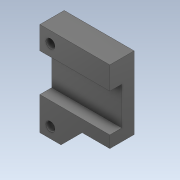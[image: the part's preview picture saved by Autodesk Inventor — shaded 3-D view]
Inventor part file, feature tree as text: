
AUTODESK INVENTOR PART (.ipt)
format: ipt  version: 2020 (Build 240168000, 168)  size: 666,112 bytes
history: native  units: mm
features: extrude x31, sketch x29, projected_geometry x21, reference x8, other x5, chamfer x4, plane x1, hole x1
ambient origin geometry x8: Origin, YZ Plane, XZ Plane, XY Plane, X Axis, Y Axis, Z Axis, Center Point
bodies: Solid1 (feature_tree)
feature tree (100):
  extrude  "Extrusion1"  Depth=45.0mm
  plane  "Work Plane1"
  extrude  "Extrusion2"  Depth=18.0mm
  extrude  "Extrusion3"  Depth=2.0mm TaperAngle=0.0deg
  extrude  "Extrusion4"  TaperAngle=0.0deg  [1 undecoded]
  extrude  "Extrusion5"  Depth=50.1mm TaperAngle=0.0deg
  sketch  "Sketch6"  dims[d14=7.199887mm d15=3.599976mm]
  extrude  "Extrusion6"  Depth=3.599976mm
  extrude  "Extrusion7"  Depth=0.15mm
  extrude  "Extrusion8"  Depth=0.15mm
  extrude  "Extrusion10"  Depth=15.9mm TaperAngle=0.0deg
  extrude  "Extrusion11"  Depth=23.15mm
  extrude  "Extrusion12"  Depth=3.925mm
  extrude  "Extrusion13"  Depth=5.15mm
  sketch  "Sketch14"  dims[d29=2.525mm d30=5.15mm]
  extrude  "Extrusion14"  Depth=12.55mm
  extrude  "Extrusion15"  Depth=2.75mm TaperAngle=0.0deg
  hole  "Hole1"  [1 undecoded]
  extrude  "Extrusion16"  Depth=3.925mm
  extrude  "Extrusion18"  Depth=23.15mm
  extrude  "Extrusion20"  Depth=10.0mm
  extrude  "Extrusion21"  Depth=0.0mm
  extrude  "Extrusion22"  TaperAngle=0.0deg  [1 undecoded]
  chamfer  "Chamfer1"  Distance=12.55mm
  extrude  "Extrusion23"  Depth=10.0mm
  extrude  "Extrusion24"  Depth=0.5mm
  chamfer  "Chamfer2"  Distance=17.225mm
  extrude  "Extrusion25"  Depth=4.0mm TaperAngle=0.0deg
  extrude  "Extrusion26"  Depth=0.5mm
  extrude  "Extrusion28"  Depth=10.925mm
  extrude  "Extrusion31"  Depth=0.5mm TaperAngle=0.0deg
  extrude  "Extrusion32"  Depth=0.5mm
  extrude  "Extrusion35"  Depth=0.5mm TaperAngle=0.0deg
  extrude  "Extrusion36"  Depth=0.5mm
  extrude  "Extrusion37"  Depth=0.5mm
  extrude  "Extrusion38"  Depth=0.5mm
  chamfer  "Chamfer4"  Distance=53.1mm
  chamfer  "Chamfer6"  Distance=53.1mm
  extrude  "Extrusion39"  Depth=0.5mm
  sketch  "Sketch1"  dims[d0=18.0mm d1=45.0mm]
  reference  "Reference1"
  sketch  "Sketch2"  dims[d2=45.0mm d3=18.0mm]
  reference  "Reference2"
  sketch  "Sketch3"  dims[d4=18.0mm d5=51.1mm d6=2.0mm d7=0.0mm d8=0.0mm]
  reference  "Reference3"
  reference  "Reference4"
  reference  "Reference5"
  reference  "Reference6"
  reference  "Reference7"
  reference  "Reference8"
  sketch  "Sketch4"  dims[d9=37.3mm d10=0.0mm]
  sketch  "Sketch5"  dims[d11=35.0mm d12=50.1mm d13=0.0mm]
  sketch  "Sketch8"  dims[d16=0.15mm d17=0.15mm]
  sketch  "Sketch10"  dims[d18=0.15mm d19=0.15mm]
  sketch  "Sketch11"  dims[d20=5.4mm d21=0.0mm d22=15.9mm d23=0.0mm]
  sketch  "Sketch12"  dims[d24=6.5mm d25=0.0mm d26=23.15mm]
  sketch  "Sketch13"  dims[d27=12.55mm d28=3.925mm]
  sketch  "Sketch15"  dims[d31=5.15mm d32=12.55mm]
  sketch  "Sketch17"  dims[d33=40.75mm d34=0.0mm d35=2.75mm d36=0.0mm]
  sketch  "Sketch19"  dims[d43=11.85mm d44=23.15mm]
  projected_geometry  "Projected Loop1"
  sketch  "Sketch21"  dims[d45=3.925mm d46=2.525mm]
  projected_geometry  "Projected Loop3"
  sketch  "Sketch22"  dims[d47=12.55mm d48=23.15mm]
  sketch  "Sketch23"  dims[d49=10.05mm d50=0.0mm d54=10.0mm]
  projected_geometry  "Projected Loop4"
  projected_geometry  "Projected Loop5"
  projected_geometry  "Projected Loop6"
  projected_geometry  "Projected Loop7"
  sketch  "Sketch24"  dims[d55=0.0mm d56=0.0mm]
  projected_geometry  "Projected Loop8"
  sketch  "Sketch25"  dims[d57=19.0mm d58=0.0mm]
  projected_geometry  "Projected Loop9"
  projected_geometry  "Projected Loop10"
  projected_geometry  "Projected Loop11"
  projected_geometry  "Projected Loop12"
  sketch  "Sketch26"  dims[d59=8.8mm]
  projected_geometry  "Projected Loop13"
  sketch  "Sketch27"  dims[d60=5.925mm]
  projected_geometry  "Projected Loop14"
  sketch  "Sketch29"  dims[d61=2.525mm]
  projected_geometry  "Projected Loop16"
  sketch  "Sketch32"  dims[d62=23.15mm]
  projected_geometry  "Projected Loop19"
  sketch  "Sketch33"  dims[d63=15.075mm]
  projected_geometry  "Projected Loop20"
  sketch  "Sketch36"  dims[d64=23.15mm]
  projected_geometry  "Projected Loop23"
  projected_geometry  "Projected Loop24"
  projected_geometry  "Projected Loop25"
  sketch  "Sketch38"  dims[d65=6.05mm]
  projected_geometry  "Projected Loop26"
  sketch  "Sketch39"  dims[d66=23.15mm d67=12.55mm d68=0.0mm]
  projected_geometry  "Projected Loop27"
  sketch  "Sketch40"  dims[d72=8.8mm d73=10.0mm d74=10.2mm d75=17.225mm d76=4.0mm d77=0.0mm d78=3.85mm d79=10.925mm d80=5.0mm d81=0.0mm d82=0.765mm d83=2.7mm d84=0.0mm d85=18.0mm d86=5.0mm d87=5.0mm d88=53.1mm d89=0.0mm d90=53.1mm d91=0.0mm d92=3.0mm d93=6.0mm d94=4.0mm d95=2.0mm d96=90.0deg d97=40.0mm d98=0.0mm d99=3.1mm d100=2.4mm d101=0.0mm d105=3.1mm d106=2.4mm d107=0.0mm d112=8.0mm d113=24.0mm d114=3.0mm d115=26.0mm d116=3.0mm d117=4.0mm d118=4.0mm d119=12.0mm d120=10.0mm d121=0.0mm d122=3.1mm d123=3.1mm d124=2.4mm d125=0.0mm d126=37.142391mm d127=15.292019mm d128=67.65mm d129=0.0mm d130=3.0mm d131=2.0mm d132=45.0deg d133=20.0mm d134=18.0mm d135=4.5mm d136=6.0mm d137=6.0mm d138=1.5mm d139=1.5mm d140=1.5mm d141=27.781995mm d142=9.376677mm d143=25.5mm d144=3.376677mm d145=25.5mm d146=2.623323mm d147=25.5mm d148=90.0deg d149=25.571384mm d150=25.571384mm d151=0.023277mm d152=2.273277mm d153=6.349941mm d154=0.020391mm d155=0.026321mm d156=25.5mm d157=9.0mm d158=25.5mm d159=6.75mm d160=30.0mm d161=6.75mm d162=25.5mm d163=5.25mm d164=30.0mm d165=5.25mm d166=25.5mm d167=0.75mm d168=30.0mm d169=0.75mm d170=25.5mm d171=0.75mm d172=30.0mm d173=0.75mm d174=25.5mm d175=5.25mm d176=30.0mm d177=5.25mm d178=25.5mm d179=6.75mm d180=30.0mm d181=6.75mm d182=34.392739mm d183=25.5mm d184=9.0mm d185=34.394624mm d186=50.0mm d187=18.0mm d188=2.0mm d189=0.0mm d190=1.5mm d191=1.5mm d192=4.5mm d193=10.0mm d194=10.0mm d195=6.0mm d196=0.0mm d197=2.0mm d198=2.0mm d199=45.0deg d200=7.0mm d201=7.0mm d202=0.0mm d203=6.0mm d204=0.0mm d211=5.0mm d212=0.0mm d225=7.0mm d226=3.0mm d227=19.5mm d228=0.0mm d229=6.1mm d230=2.0mm d231=0.0mm d238=68.25mm d239=0.0mm d240=5.6mm d241=5.6mm d242=2.0mm d243=0.0mm d244=7.525mm d245=5.6mm d246=3.5mm d247=2.5mm d248=0.0mm d249=3.0mm d250=2.0mm d251=0.0mm d252=7.0mm d253=2.0mm d254=45.0deg d258=2.0mm d259=2.0mm d260=45.0deg d261=10.1mm d262=10.0mm d263=0.0mm d108=0.5mm d109=0.872665mm]
  parser-record x1  (decoder bookkeeping rows leaked as tree rows — omitted from the tree; the rows remain in map.json)
  other  "Demo2.0004.iam"
  other  "Bearing:2"
  other  "Rolling bearing GB/T 7218-1995 Type FSN 70000-Z F 623-Z:1"
  other  "servo horn 1:1"
note: 3 required parameter values undecoded (feature->parameter linkage not recoverable at this tier; creation-order binding heuristic only, values carry confidence <= 0.55)
note: 1 file-system path scrubbed to <path> (originals preserved in map.json)
